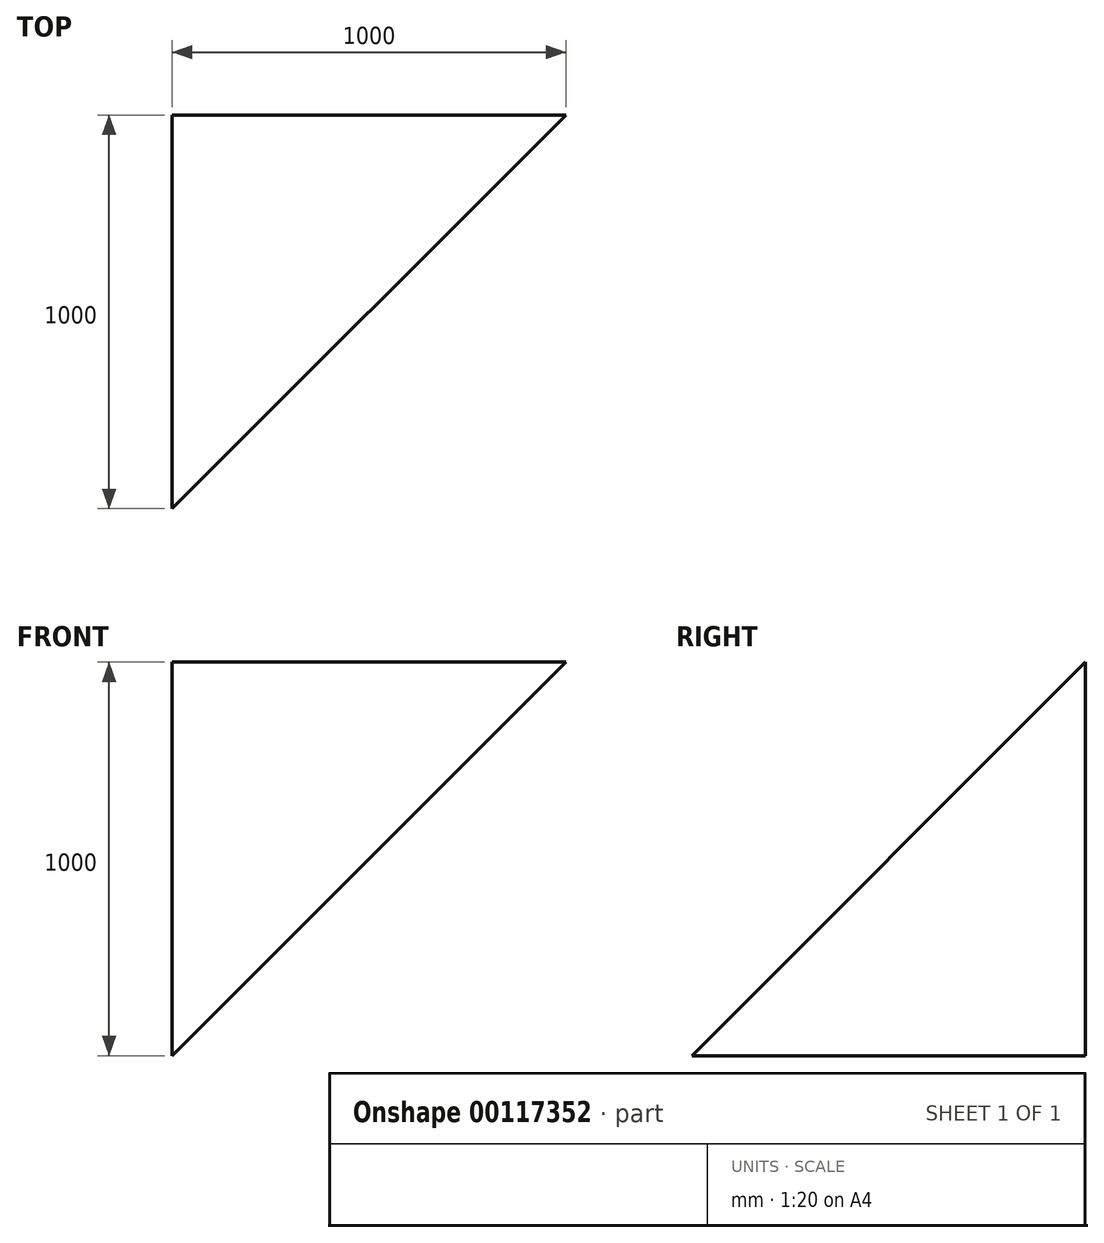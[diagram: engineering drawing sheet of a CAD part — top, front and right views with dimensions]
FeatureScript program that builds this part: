
annotation { "Feature Type Name" : "Feature", "Feature Type Description" : "" }
export const myFeature = defineFeature(function(context is Context, id is Id, definition is map)
    precondition{}
    {
        {
            var Q0;
            Q0=qCreatedBy(makeId("Top.planeOp"),FACE);
            var sketch = newSketch(context, id + "F0", { "sketchPlane" : qUnion([Q0])});
            skLineSegment(sketch, "E0.bottom", {"start": v(0, 0) * mm, "end": v(1000, 0) * mm});
            skLineSegment(sketch, "E0.top", {"start": v(0, 1000) * mm, "end": v(1000, 1000) * mm});
            skLineSegment(sketch, "E0.left", {"start": v(0, 0) * mm, "end": v(0, 1000) * mm});
            skLineSegment(sketch, "E0.right", {"start": v(1000, 0) * mm, "end": v(1000, 1000) * mm});
            skSolve(sketch);
        }
        {
            var Q0;
            Q0=makeQuery(id+"F0.imprint","IMPRINT",FACE,{"disambiguationData":[TD([[makeQuery(id+"F0.imprint","IMPRINT",EDGE,{"derivedFrom":sQuery(id+"F0.wireOp",EDGE,"E0.bottom")}),1.0]])]});
            extrude(context, id + "F1", {"entities" : qUnion([Q0]), "depth" : 1000 * mm});
        }
        {
            var Q0;
            Q0=makeQuery(id+"F1.opExtrude","SWEPT_FACE",FACE,{"disambiguationData":[OSD([sQuery(id+"F0.wireOp",EDGE,"E0.right")])]});
            var sketch = newSketch(context, id + "F2", { "sketchPlane" : qUnion([Q0])});
            skLineSegment(sketch, "E1", {"start": v(1000, 1000) * mm, "end": v(0, 0) * mm});
            skLineSegment(sketch, "E2", {"start": v(0, 0) * mm, "end": v(0, 1000) * mm});
            skLineSegment(sketch, "E3", {"start": v(0, 1000) * mm, "end": v(1000, 1000) * mm});
            skSolve(sketch);
        }
        {
            var Q0;
            Q0=makeQuery(id+"F1.opExtrude","SWEPT_FACE",FACE,{"disambiguationData":[OSD([sQuery(id+"F0.wireOp",EDGE,"E0.bottom")])]});
            var sketch = newSketch(context, id + "F3", { "sketchPlane" : qUnion([Q0])});
            skLineSegment(sketch, "E4", {"start": v(1000, 1000) * mm, "end": v(0, 0) * mm});
            skLineSegment(sketch, "E5", {"start": v(0, 0) * mm, "end": v(1000, 0) * mm});
            skLineSegment(sketch, "E6", {"start": v(1000, 0) * mm, "end": v(1000, 1000) * mm});
            skSolve(sketch);
        }
        {
            var Q0;
            Q0 = qSketchRegion(id + "F2", true);
            extrude(context, id + "F4", {"entities" : qUnion([Q0]), "operationType" : NewBodyOperationType.REMOVE, "endBound" : BoundingType.THROUGH_ALL, "oppositeDirection" : true, "depth" : 25 * mm});
        }
        {
            var Q0;
            Q0 = qSketchRegion(id + "F3", true);
            extrude(context, id + "F5", {"entities" : qUnion([Q0]), "operationType" : NewBodyOperationType.REMOVE, "endBound" : BoundingType.THROUGH_ALL, "oppositeDirection" : true, "depth" : 25 * mm});
        }
    });
